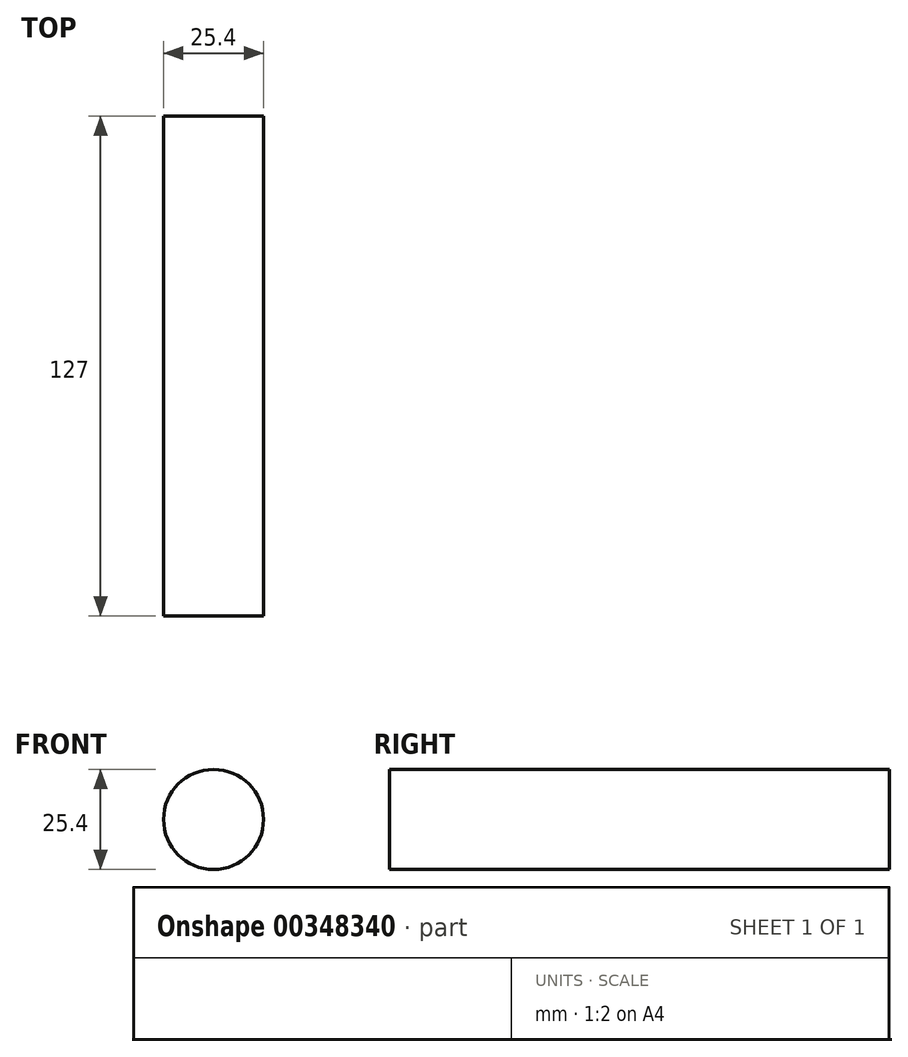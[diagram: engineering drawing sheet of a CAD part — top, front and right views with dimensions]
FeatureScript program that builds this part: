
annotation { "Feature Type Name" : "Feature", "Feature Type Description" : "" }
export const myFeature = defineFeature(function(context is Context, id is Id, definition is map)
    precondition{}
    {
        {
            var Q0;
            Q0=qCreatedBy(makeId("Front.planeOp"),FACE);
            var sketch = newSketch(context, id + "F0", { "sketchPlane" : qUnion([Q0])});
            skCircle(sketch, "E0", {"center": v(0, 0) * mm, "radius": 12.7 * mm});
            skSolve(sketch);
        }
        {
            var Q0;
            Q0=makeQuery(id+"F0.imprint","IMPRINT",FACE,{"disambiguationData":[TD([[makeQuery(id+"F0.imprint","IMPRINT",EDGE,{"derivedFrom":sQuery(id+"F0.wireOp",EDGE,"E0")}),1.0]])]});
            extrude(context, id + "F1", {"entities" : qUnion([Q0]), "depth" : 127 * mm});
        }
    });
